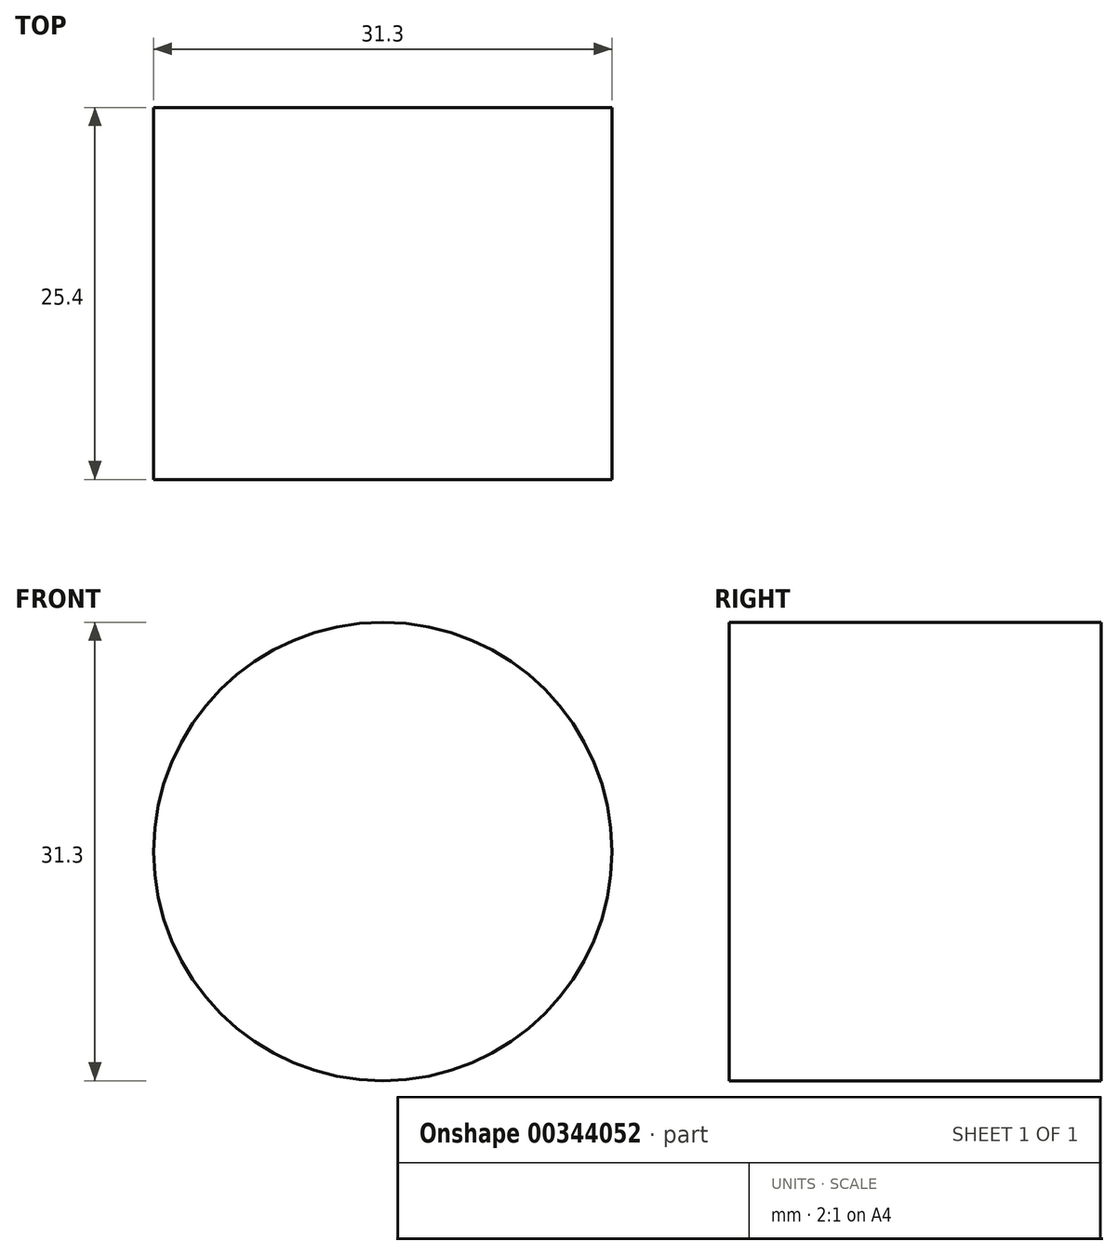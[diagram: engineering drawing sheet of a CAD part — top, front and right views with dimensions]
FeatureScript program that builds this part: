
annotation { "Feature Type Name" : "Feature", "Feature Type Description" : "" }
export const myFeature = defineFeature(function(context is Context, id is Id, definition is map)
    precondition{}
    {
        {
            var Q0;
            Q0=qCreatedBy(makeId("Front.planeOp"),FACE);
            var sketch = newSketch(context, id + "F0", { "sketchPlane" : qUnion([Q0])});
            skCircle(sketch, "E0", {"center": v(0, 0) * mm, "radius": 15.65 * mm});
            skSolve(sketch);
        }
        {
            var Q0;
            Q0=qCreatedBy(makeId("Front.planeOp"),FACE);
            var sketch = newSketch(context, id + "F1", { "sketchPlane" : qUnion([Q0])});
            skCircle(sketch, "E1", {"center": v(0, 0) * mm, "radius": 10.5 * mm});
            skSolve(sketch);
        }
        {
            var Q0;
            Q0=makeQuery(id+"F1.imprint","IMPRINT",FACE,{"disambiguationData":[TD([[makeQuery(id+"F1.imprint","IMPRINT",EDGE,{"derivedFrom":sQuery(id+"F1.wireOp",EDGE,"E1")}),1.0]])]});
            extrude(context, id + "F2", {"entities" : qUnion([Q0]), "depth" : 25.4 * mm});
        }
        {
            var Q0;
            Q0=makeQuery(id+"F0.imprint","IMPRINT",FACE,{"disambiguationData":[TD([[makeQuery(id+"F0.imprint","IMPRINT",EDGE,{"derivedFrom":sQuery(id+"F0.wireOp",EDGE,"E0")}),1.0]])]});
            extrude(context, id + "F3", {"entities" : qUnion([Q0]), "operationType" : NewBodyOperationType.ADD, "depth" : 25.4 * mm});
        }
    });
